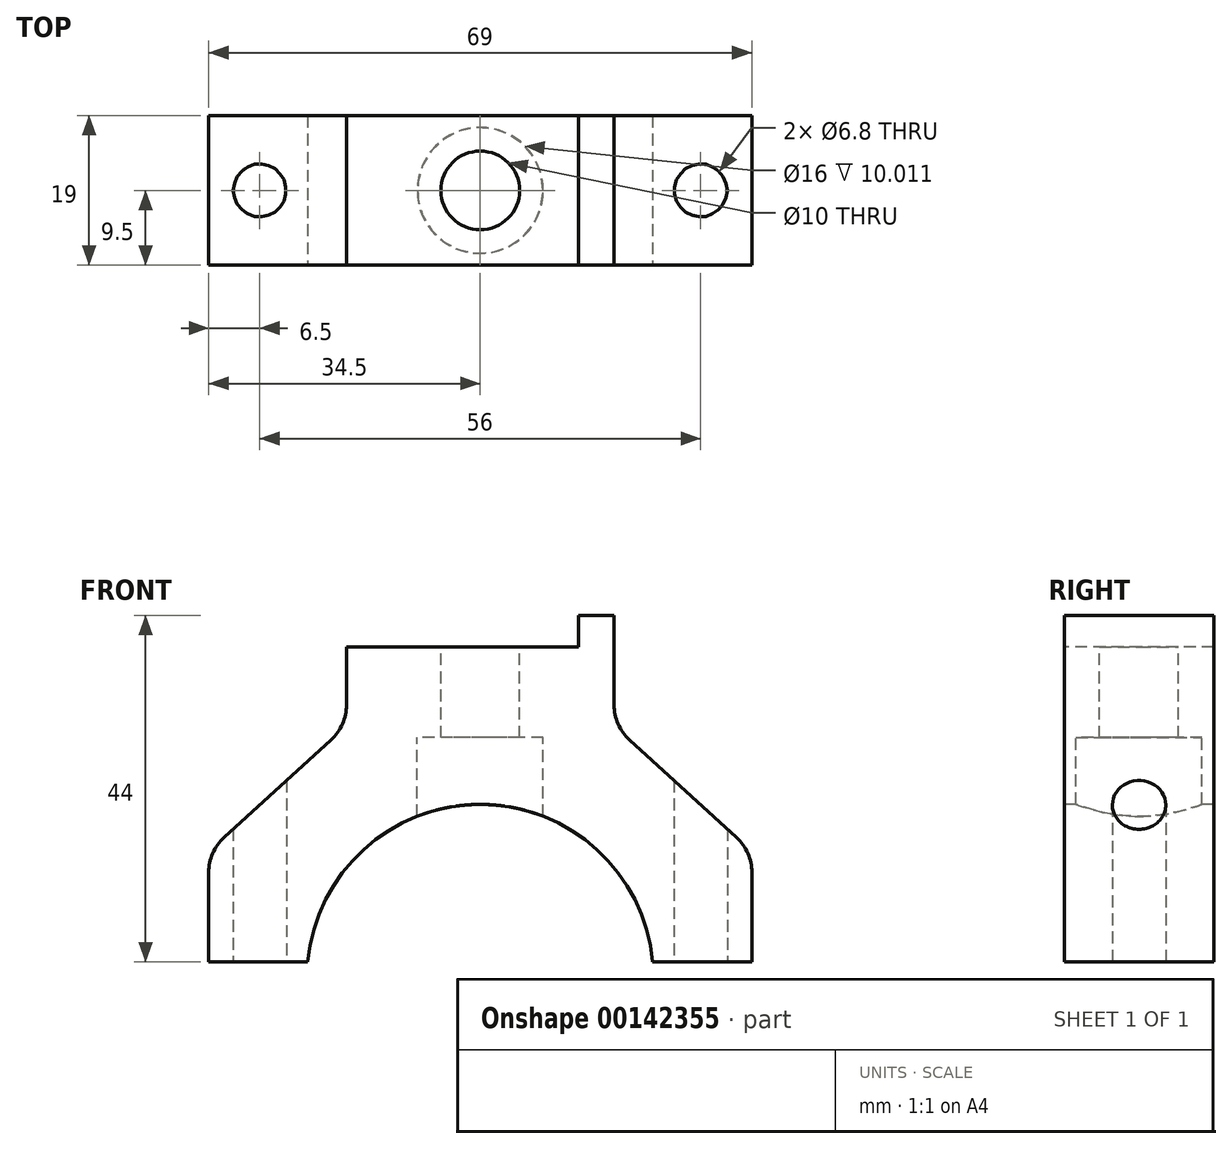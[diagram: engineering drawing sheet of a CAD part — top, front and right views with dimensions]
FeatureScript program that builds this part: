
annotation { "Feature Type Name" : "Feature", "Feature Type Description" : "" }
export const myFeature = defineFeature(function(context is Context, id is Id, definition is map)
    precondition{}
    {
        {
            var Q0;
            Q0=qCreatedBy(makeId("Front.planeOp"),FACE);
            var sketch = newSketch(context, id + "F0", { "sketchPlane" : qUnion([Q0])});
            skLineSegment(sketch, "E0", {"start": v(0, 0) * mm, "end": v(0, 57.31) * mm, "construction": true});
            skLineSegment(sketch, "E1", {"start": v(0, 0) * mm, "end": v(0, -51.6) * mm, "construction": true});
            skLineSegment(sketch, "E2", {"start": v(0, 0) * mm, "end": v(-44.18, 0) * mm, "construction": true});
            skLineSegment(sketch, "E3", {"start": v(0, 0) * mm, "end": v(47.32, 0) * mm, "construction": true});
            skLineSegment(sketch, "E4", {"start": v(-21.9, 2) * mm, "end": v(-34.5, 2) * mm});
            skArc(sketch, "E5", {"start": v(-21.9, 2) * mm, "mid": v(-14.83, 16.25) * mm, "end": v(0, 22) * mm});
            skLineSegment(sketch, "E6", {"start": v(-34.5, 2) * mm, "end": v(-34.5, 16) * mm});
            skLineSegment(sketch, "E7", {"start": v(-34.5, 16) * mm, "end": v(-17, 32) * mm});
            skLineSegment(sketch, "E8", {"start": v(-17, 32) * mm, "end": v(-17, 46) * mm});
            skLineSegment(sketch, "E9", {"start": v(-17, 46) * mm, "end": v(0, 46) * mm});
            skLineSegment(sketch, "E10", {"start": v(0, 46) * mm, "end": v(0, 22) * mm});
            skSolve(sketch);
        }
        {
            var Q0;
            Q0=makeQuery(id+"F0.imprint","IMPRINT",FACE,{"disambiguationData":[TD([[makeQuery(id+"F0.imprint","IMPRINT",EDGE,{"derivedFrom":sQuery(id+"F0.wireOp",EDGE,"E4")}),-1.0]])]});
            extrude(context, id + "F1", {"entities" : qUnion([Q0]), "endBound" : BoundingType.SYMMETRIC, "oppositeDirection" : true, "depth" : 19 * mm});
        }
        {
            var Q0;
            Q0=makeQuery(id+"F1.opExtrude","SWEPT_FACE",FACE,{"disambiguationData":[OSD([sQuery(id+"F0.wireOp",EDGE,"E4")])]});
            var sketch = newSketch(context, id + "F2", { "sketchPlane" : qUnion([Q0])});
            skCircle(sketch, "E11", {"center": v(-28, 0) * mm, "radius": 3.4 * mm});
            skSolve(sketch);
        }
        {
            var Q0;
            Q0=makeQuery(id+"F2.imprint","IMPRINT",FACE,{"disambiguationData":[TD([[makeQuery(id+"F2.imprint","IMPRINT",EDGE,{"derivedFrom":sQuery(id+"F2.wireOp",EDGE,"E11")}),1.0]])]});
            extrude(context, id + "F3", {"entities" : qUnion([Q0]), "operationType" : NewBodyOperationType.REMOVE, "endBound" : BoundingType.UP_TO_NEXT, "oppositeDirection" : true, "depth" : 25 * mm});
        }
        {
            var Q0;
            Q0=makeQuery(id+"F1.opExtrude","SWEPT_BODY",BODY,{"disambiguationData":[OSD([sQuery(id+"F0.wireOp",EDGE,"E4"),sQuery(id+"F0.wireOp",EDGE,"E5"),sQuery(id+"F0.wireOp",EDGE,"E6"),sQuery(id+"F0.wireOp",EDGE,"E7"),sQuery(id+"F0.wireOp",EDGE,"E8"),sQuery(id+"F0.wireOp",EDGE,"E9"),sQuery(id+"F0.wireOp",EDGE,"E10")])]});
            var Q1;
            Q1=qCreatedBy(makeId("Right.planeOp"),FACE);
            mirror(context, id + "F4", {"operationType" : NewBodyOperationType.ADD, "entities" : qUnion([Q0]), "mirrorPlane" : qUnion([Q1])});
        }
        {
            var Q0;
            {var subQ0=makeQuery(id+"F1.opExtrude","SWEPT_FACE",FACE,{"disambiguationData":[OSD([sQuery(id+"F0.wireOp",EDGE,"E9")])]});Q0=makeQuery(id+"F4.boolean.opBoolean","MERGE",FACE,{"derivedFrom":[subQ0,makeQuery(id+"F4.opPattern","COPY",FACE,{"derivedFrom":subQ0,"instanceName":"1"})]});}
            var sketch = newSketch(context, id + "F5", { "sketchPlane" : qUnion([Q0])});
            skLineSegment(sketch, "E12", {"start": v(-17, 9.5) * mm, "end": v(12.5, 9.5) * mm});
            skLineSegment(sketch, "E13", {"start": v(12.5, 9.5) * mm, "end": v(12.5, -9.5) * mm});
            skLineSegment(sketch, "E14", {"start": v(12.5, -9.5) * mm, "end": v(-17, -9.5) * mm});
            skLineSegment(sketch, "E15", {"start": v(-17, -9.5) * mm, "end": v(-17, 9.5) * mm});
            skSolve(sketch);
        }
        {
            var Q0;
            Q0=makeQuery(id+"F5.imprint","IMPRINT",FACE,{"disambiguationData":[TD([[makeQuery(id+"F5.imprint","IMPRINT",EDGE,{"derivedFrom":sQuery(id+"F5.wireOp",EDGE,"E12")}),-1.0]])]});
            extrude(context, id + "F6", {"entities" : qUnion([Q0]), "operationType" : NewBodyOperationType.REMOVE, "oppositeDirection" : true, "depth" : 4 * mm});
        }
        {
            var Q0;
            Q0=makeQuery(id+"F6.boolean.opBoolean","COPY",FACE,{"derivedFrom":makeQuery(id+"F6.opExtrude","CAP_FACE",FACE,{"disambiguationData":[OSD([sQuery(id+"F5.wireOp",EDGE,"E12"),sQuery(id+"F5.wireOp",EDGE,"E13"),sQuery(id+"F5.wireOp",EDGE,"E14"),sQuery(id+"F5.wireOp",EDGE,"E15")])],"isStart":false})});
            var sketch = newSketch(context, id + "F7", { "sketchPlane" : qUnion([Q0])});
            skCircle(sketch, "E16", {"center": v(0, 0) * mm, "radius": 8 * mm});
            skSolve(sketch);
        }
        {
            var Q0;
            Q0=makeQuery(id+"F7.imprint","IMPRINT",FACE,{"disambiguationData":[TD([[makeQuery(id+"F7.imprint","IMPRINT",EDGE,{"derivedFrom":sQuery(id+"F7.wireOp",EDGE,"E16")}),1.0]])]});
            extrude(context, id + "F8", {"entities" : qUnion([Q0]), "operationType" : NewBodyOperationType.REMOVE, "endBound" : BoundingType.THROUGH_ALL, "oppositeDirection" : true, "depth" : 25 * mm});
        }
        {
            var Q0;
            Q0=makeQuery(id+"F6.boolean.opBoolean","COPY",FACE,{"derivedFrom":makeQuery(id+"F6.opExtrude","CAP_FACE",FACE,{"disambiguationData":[OSD([sQuery(id+"F5.wireOp",EDGE,"E12"),sQuery(id+"F5.wireOp",EDGE,"E13"),sQuery(id+"F5.wireOp",EDGE,"E14"),sQuery(id+"F5.wireOp",EDGE,"E15")])],"isStart":false})});
            var sketch = newSketch(context, id + "F9", { "sketchPlane" : qUnion([Q0])});
            skLineSegment(sketch, "E17", {"start": v(0, 0) * mm, "end": v(-12.78, 0) * mm, "construction": true});
            skLineSegment(sketch, "E18", {"start": v(0, 0) * mm, "end": v(10.5, 0) * mm, "construction": true});
            skLineSegment(sketch, "E19", {"start": v(0, 0) * mm, "end": v(0, 8.7) * mm, "construction": true});
            skLineSegment(sketch, "E20", {"start": v(0, 0) * mm, "end": v(0, -9.5) * mm, "construction": true});
            skCircle(sketch, "E21", {"center": v(0, 0) * mm, "radius": 5 * mm});
            skCircle(sketch, "E22", {"center": v(0, 0) * mm, "radius": 8 * mm});
            skSolve(sketch);
        }
        {
            var Q0;
            Q0=makeQuery(id+"F9.imprint","IMPRINT",FACE,{"disambiguationData":[TD([[makeQuery(id+"F9.imprint","IMPRINT",EDGE,{"derivedFrom":sQuery(id+"F9.wireOp",EDGE,"E21")}),-1.0]])]});
            extrude(context, id + "F10", {"entities" : qUnion([Q0]), "operationType" : NewBodyOperationType.ADD, "oppositeDirection" : true, "depth" : 11.5 * mm});
        }
        {
            var Q0;
            Q0=makeQuery(id+"F1.opExtrude","SWEPT_EDGE",EDGE,{"disambiguationData":[OSD([sQuery(id+"F0.wireOp",EDGE,"E6"),sQuery(id+"F0.wireOp",EDGE,"E7")])]});
            var Q1;
            Q1=makeQuery(id+"F4.opPattern","COPY",EDGE,{"derivedFrom":makeQuery(id+"F1.opExtrude","SWEPT_EDGE",EDGE,{"disambiguationData":[OSD([sQuery(id+"F0.wireOp",EDGE,"E6"),sQuery(id+"F0.wireOp",EDGE,"E7")])]}),"instanceName":"1"});
            var Q2;
            Q2=makeQuery(id+"F1.opExtrude","SWEPT_EDGE",EDGE,{"disambiguationData":[OSD([sQuery(id+"F0.wireOp",EDGE,"E7"),sQuery(id+"F0.wireOp",EDGE,"E8")])]});
            var Q3;
            Q3=makeQuery(id+"F4.opPattern","COPY",EDGE,{"derivedFrom":makeQuery(id+"F1.opExtrude","SWEPT_EDGE",EDGE,{"disambiguationData":[OSD([sQuery(id+"F0.wireOp",EDGE,"E7"),sQuery(id+"F0.wireOp",EDGE,"E8")])]}),"instanceName":"1"});
            fillet(context, id + "F11", {"entities" : qUnion([Q0, Q1, Q2, Q3]), "radius" : 6 * mm, "tangentPropagation" : true, "allowEdgeOverflow" : false});
        }
    });
